# Revit family: MS814224CUFG
name_source: partatom
category: Plumbing Fixtures
revit_build: Autodesk Revit 2014 (Build: 20130308_1515(x64)
units: mm (PartAtom-declared; Revit-internal decimal feet)

## types (1)
- MS814224CUFG
    Codes/Standards = • Meets and exceeds ASME A112.19.2/CSA B45.1 • Certifications: IAPMO(cUPC), EPA Watersense, State of Massachusetts , City of Los Angeles, and others • Code compliance: UPC, IPC, NSPC, NPC Canada, and others  • Legislative Compliance: California AB715, California Green Building Code, City of Los  Angeles Water Efficiency Ordinance, Buy American Act (BAA)  • ADA compliant (when installed with trip lever located on the approach side)
    Colors/Finishes = Standard #01 Cotton #03 Bone #11 Colonial White #12 Sedona Beige #51 Ebony (without CeFiONtect)
    Manufacturer = TOTO USA
    Model = MS814224CUF9(G)
    Specifications = Water Use 1.0 GPF/3.8LPF Flush System Tornado Flush Min. Water Pressure 8 psi (static) Water Surface 9" x 6-3/4" Trap Diameter 2-1/8" Rough-in 12" Trap Seal 2-1/4" Warranty One Year Limited Warranty Material	Vitreous china Shipping Weight 103 lbs
Shipping Dimensions 32"L x 20"W x 17-3/4"H1 x 28-3/4"H2
    trap seal = 0' - 2 1/8"

## geometry (parser evidence)
native form markers: Sweep x11
no freeform markers — native parametric forms only
